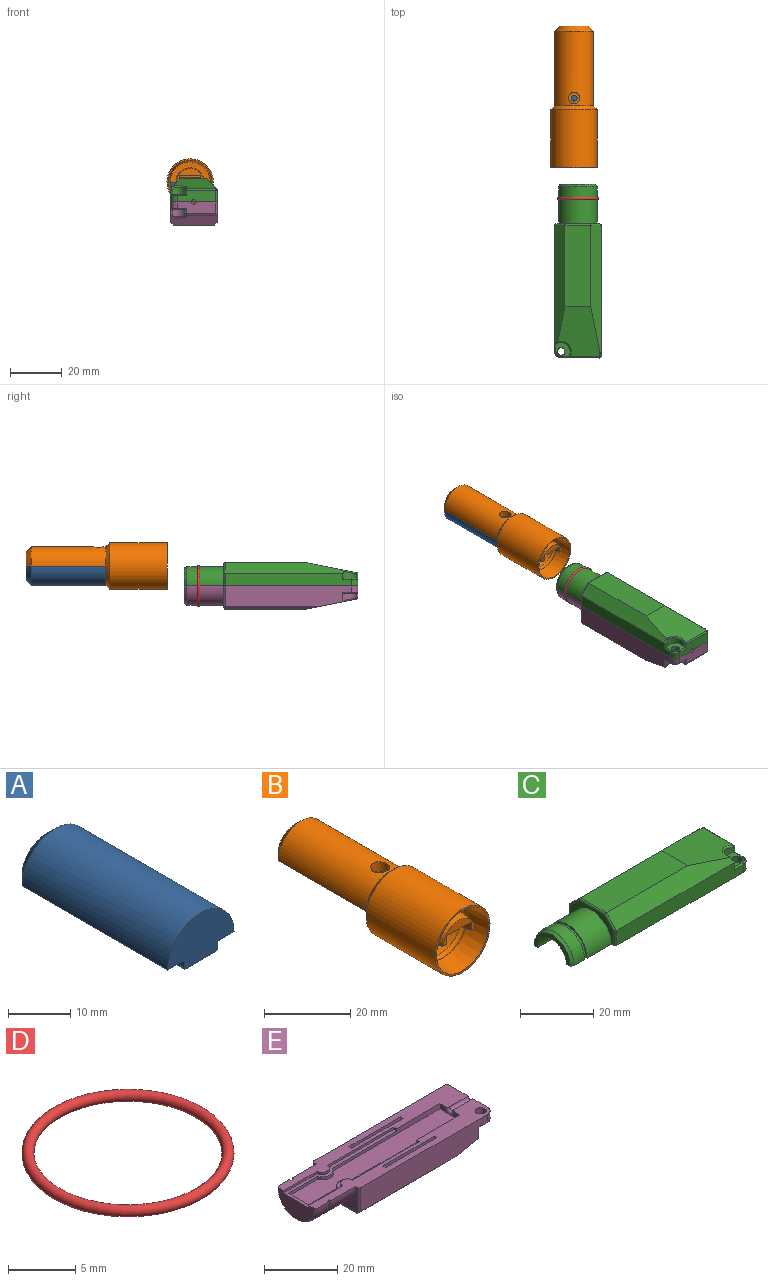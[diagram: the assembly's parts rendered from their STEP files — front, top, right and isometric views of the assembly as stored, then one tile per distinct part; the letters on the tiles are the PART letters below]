
ASSEMBLY  parts=5 mates=4
PART A: 19 faces, bbox 15x35x9.3 mm
  f0: plane 11x5.5mm, normal (0,1,0), area 43mm2, adj f1,f4,f13
  f1: plane 35x15mm, normal (0,0,-1), area 426.5mm2, adj f0,f2,f3,f4,f5,f6,f7,f8
  f2: cylinder r=7.5mm len=33mm, axis (0,1,0), area 777.5mm2, adj f1,f3,f13
  f3: plane 15x9.3mm, normal (0,-1,0), area 101.9mm2, adj f1,f2,f5,f6,f12,f17,f18
  f4: cylinder r=1.7mm len=17mm, axis (0,1,0), area 85mm2, adj f0,f1,f14
  f5: plane 11x1.2mm, normal (1,0,0), area 13.2mm2, adj f1,f3,f11,f18
  f6: plane 11x1.2mm, normal (-1,0,0), area 13.2mm2, adj f1,f3,f7,f17
  f7: plane 1.8x1mm, normal (0,1,0), area 1.7mm2, adj f1,f6,f8,f12,f17
  f8: plane 9x1.8mm, normal (1,0,0), area 16.2mm2, adj f1,f7,f9,f12
  f9: plane 5.6x1.8mm, normal (0,1,0), area 10.1mm2, adj f1,f8,f10,f12
  f10: plane 9x1.8mm, normal (-1,0,0), area 16.2mm2, adj f1,f9,f11,f12
  f11: plane 1.8x1mm, normal (0,1,0), area 1.7mm2, adj f1,f5,f10,f12,f18
  f12: plane 11x7.2mm, normal (0,0,-1), area 28.8mm2, adj f3,f7,f8,f9,f10,f11,f17,f18
  f13: cone r=7.5mm half-angle=45deg, axis (0,-1,0), area 57.8mm2, adj f0,f1,f2
  f14: plane 3.4x1.7mm, normal (0,0.71,-0.71), area 6.4mm2, adj f1,f4
  f15: cylinder r=1.05mm len=6mm, axis (0,0,-1), area 39.6mm2, adj f1,f16
  f16: plane 2.1x2.1mm, normal (0,0,-1), area 3.5mm2, adj f15
  f17: plane 11x0.6mm, normal (-0.95,0,-0.32), area 7mm2, adj f3,f6,f7,f12
  f18: plane 11x0.6mm, normal (0.95,0,-0.32), area 7mm2, adj f3,f5,f11,f12
PART B: 29 faces, bbox 18x54.9x18 mm
  f0: plane 15.6x15.6mm, normal (0,-1,0), area 52.9mm2, adj f4,f7,f8,f21,f28
  f1: cone r=9mm half-angle=45deg, axis (0,-1,0), area 106.6mm2, adj f3,f4,f7,f20,f28
  f2: cylinder r=1.7mm len=8.6mm, axis (0,1,0), area 45.1mm2, adj f4,f5,f7,f11,f25
  f3: cylinder r=7.5mm len=28.9mm, axis (0,1,0), area 665.5mm2, adj f1,f4,f7,f13,f15
  f4: plane 50.7x5.9mm, normal (0,0,-1), area 174.5mm2, adj f0,f1,f2,f3,f5,f8,f9,f11
  f5: plane 11x5.5mm, normal (0,1,0), area 43mm2, adj f2,f4,f7,f13
  f6: plane 10.38x4.9mm, normal (0,-1,0), area 20.2mm2, adj f9,f10,f12,f17,f18,f19
  f7: plane 50.7x5.9mm, normal (0,0,-1), area 174.5mm2, adj f0,f1,f2,f3,f5,f8,f10,f11
  f8: cylinder r=5.5mm len=11mm, axis (0,1,0), area 186.6mm2, adj f0,f4,f7,f17
  f9: plane 45.1x2.7mm, normal (-1,0,0), area 121.3mm2, adj f4,f6,f11,f12,f18
  f10: plane 45.1x2.7mm, normal (1,0,0), area 121.3mm2, adj f6,f7,f11,f12,f19
  f11: plane 8x2.7mm, normal (0,-1,0), area 17.1mm2, adj f2,f4,f7,f9,f10,f12
  f12: plane 45.1x8mm, normal (0,0,-1), area 356.6mm2, adj f6,f9,f10,f11,f14
  f13: cone r=7.5mm half-angle=45deg, axis (0,-1,0), area 57.8mm2, adj f3,f4,f5,f7
  f14: cylinder r=1.15mm len=2.3mm, axis (0,0,-1), area 14.5mm2, adj f12,f16
  f15: cylinder r=2.2mm len=4.4mm, axis (0,0,-1), area 36.4mm2, adj f3,f16
  f16: plane 4.4x4.4mm, normal (0,0,1), area 11.1mm2, adj f14,f15
  f17: cone r=5.2mm half-angle=5.7deg, axis (0,1,0), area 49.8mm2, adj f6,f8,f18,f19
  f18: plane 3.01x1.51mm, normal (0,-0.1,-1), area 4.1mm2, adj f4,f6,f9,f17
  f19: plane 3.01x1.51mm, normal (0,-0.1,-1), area 4.1mm2, adj f6,f7,f10,f17
  f20: cylinder r=9mm len=22.5mm, axis (0,-1,0), area 1272.3mm2, adj f1,f24
  f21: cylinder r=7.8mm len=15.6mm, axis (0,-1,0), area 358.8mm2, adj f0,f22
  f22: torus R=7.3mm, axis (0,-1,0), area 85.6mm2, adj f21,f23
  f23: cone r=8.5mm half-angle=5.2deg, axis (0,-1,0), area 322.7mm2, adj f22,f24
  f24: plane 18x18mm, normal (0,-1,0), area 27.5mm2, adj f20,f23
  f25: cylinder r=0.5mm len=1mm, axis (0,0,1), area 1.5mm2, adj f2,f27
  f26: plane 0.4x0.4mm, normal (0,0,-1), area 0.1mm2, adj f27
  f27: cone r=0.2mm half-angle=45deg, axis (0,0,1), area 0.9mm2, adj f25,f26
  f28: cylinder r=7.6mm len=15.2mm, axis (0,-1,0), area 212.5mm2, adj f0,f1,f4,f7
PART C: 64 faces, bbox 67.6x18.2x10 mm
  f0: plane 67.4x18mm, normal (0,0,-1), area 609.6mm2, adj f2,f3,f4,f6,f7,f9,f10,f11
  f1: plane 5.5x5.5mm, normal (0,0,1), area 18.9mm2, adj f53,f54,f56,f57,f59,f61,f63
  f2: plane 45.1x2.2mm, normal (0,-1,0), area 99.2mm2, adj f0,f17,f18,f52
  f3: cylinder r=7.5mm len=15mm, axis (1,0,0), area 221.5mm2, adj f0,f4,f31
  f4: plane 17x8.5mm, normal (-1,0,0), area 42.4mm2, adj f0,f3,f42,f43,f44,f45,f46
  f5: plane 31.5x10mm, normal (0,0,1), area 315mm2, adj f8,f12,f13,f44
  f6: plane 49x5mm, normal (0,-1,0), area 236.3mm2, adj f0,f13,f45,f55,f56,f57
  f7: plane 51x5mm, normal (0,1,0), area 254.6mm2, adj f0,f12,f42,f47,f49
  f8: plane 19.62x16.25mm, normal (0.2,0,0.98), area 246.1mm2, adj f5,f12,f13,f48,f49,f58,f60
  f9: plane 15x4.59mm, normal (1,0,0), area 60.3mm2, adj f0,f19,f47,f48,f55,f61,f63
  f10: cylinder r=7.5mm len=15mm, axis (1,0,0), area 94.2mm2, adj f0,f32,f51
  f11: plane 14x7mm, normal (-1,0,0), area 29.5mm2, adj f0,f14,f51
  f12: plane 50.02x4mm, normal (0,0.71,0.71), area 234.4mm2, adj f5,f7,f8,f43,f49
  f13: plane 45.62x4mm, normal (0,-0.71,0.71), area 229.4mm2, adj f5,f6,f8,f46,f56,f58
  f14: cylinder r=5.5mm len=12.8mm, axis (-1,0,0), area 221.2mm2, adj f0,f11,f15
  f15: plane 11x5.5mm, normal (-1,0,0), area 47.5mm2, adj f0,f14
  f16: plane 45.1x2.2mm, normal (0,1,0), area 99.2mm2, adj f0,f17,f18,f52
  f17: plane 45.1x8mm, normal (0,0,-1), area 360.8mm2, adj f2,f16,f18,f52
  f18: plane 8x2.2mm, normal (-1,0,0), area 13.1mm2, adj f0,f2,f16,f17,f41
  f19: cylinder r=0.9mm len=7.2mm, axis (-1,0,0), area 20.4mm2, adj f0,f9,f41
  f20: plane 0.8x0.8mm, normal (-1,0,0), area 0.6mm2, adj f0,f21,f23,f38
  f21: plane 19.4x0.8mm, normal (0,1,0), area 15.5mm2, adj f0,f20,f22,f37
  f22: plane 0.8x0.8mm, normal (1,0,0), area 0.6mm2, adj f0,f21,f23,f39
  f23: plane 19.4x0.8mm, normal (0,-1,0), area 15.5mm2, adj f0,f20,f22,f40
  f24: plane 19x0.4mm, normal (0,0,-1), area 7.6mm2, adj f37,f38,f39,f40
  f25: plane 0.8x0.8mm, normal (-1,0,0), area 0.6mm2, adj f0,f26,f28,f34
  f26: plane 19.4x0.8mm, normal (0,1,0), area 15.5mm2, adj f0,f25,f27,f33
  f27: plane 0.8x0.8mm, normal (1,0,0), area 0.6mm2, adj f0,f26,f28,f35
  f28: plane 19.4x0.8mm, normal (0,-1,0), area 15.5mm2, adj f0,f25,f27,f36
  f29: plane 19x0.4mm, normal (0,0,-1), area 7.6mm2, adj f33,f34,f35,f36
  f30: cylinder r=7mm len=14mm, axis (-1,0,0), area 22mm2, adj f0,f31,f32
  f31: plane 15x7.5mm, normal (-1,0,0), area 11.4mm2, adj f0,f3,f30
  f32: plane 15x7.5mm, normal (1,0,0), area 11.4mm2, adj f0,f10,f30
  f33: plane 19.4x0.2mm, normal (0,0.71,-0.71), area 5.4mm2, adj f26,f29,f34,f35
  f34: plane 0.8x0.2mm, normal (-0.71,0,-0.71), area 0.2mm2, adj f25,f29,f33,f36
  f35: plane 0.8x0.2mm, normal (0.71,0,-0.71), area 0.2mm2, adj f27,f29,f33,f36
  f36: plane 19.4x0.2mm, normal (0,-0.71,-0.71), area 5.4mm2, adj f28,f29,f34,f35
  f37: plane 19.4x0.2mm, normal (0,0.71,-0.71), area 5.4mm2, adj f21,f24,f38,f39
  f38: plane 0.8x0.2mm, normal (-0.71,0,-0.71), area 0.2mm2, adj f20,f24,f37,f40
  f39: plane 0.8x0.2mm, normal (0.71,0,-0.71), area 0.2mm2, adj f22,f24,f37,f40
  f40: plane 19.4x0.2mm, normal (0,-0.71,-0.71), area 5.4mm2, adj f23,f24,f38,f39
  f41: torus R=1.7mm, axis (-1,0,0), area 4.7mm2, adj f0,f18,f19
  f42: cylinder r=0.5mm len=5mm, axis (0,0,1), area 3.8mm2, adj f0,f4,f7,f43
  f43: cylinder r=0.5mm len=4.35mm, axis (0,-0.71,0.71), area 4.3mm2, adj f4,f12,f42,f44
  f44: cylinder r=0.5mm len=10mm, axis (0,1,0), area 7.7mm2, adj f4,f5,f43,f46
  f45: cylinder r=0.5mm len=5mm, axis (0,0,-1), area 3.8mm2, adj f0,f4,f6,f46
  f46: cylinder r=0.5mm len=4.35mm, axis (0,-0.71,-0.71), area 4.3mm2, adj f4,f13,f44,f45
  f47: cylinder r=0.5mm len=4.59mm, axis (0,0,-1), area 3.6mm2, adj f0,f7,f9,f50
  f48: cylinder r=0.5mm len=11.54mm, axis (0,1,0), area 7.9mm2, adj f8,f9,f50,f62
  f49: cylinder r=0.5mm len=2.2mm, axis (0.98,0,-0.2), area 1.1mm2, adj f7,f8,f12,f50
  f50: sphere r=0.5mm, area 0.5mm2, adj f47,f48,f49
  f51: cone r=7mm half-angle=26.6deg, axis (1,0,0), area 25.5mm2, adj f0,f10,f11
  f52: plane 8x2.2mm, normal (1,0,0), area 17.6mm2, adj f0,f2,f16,f17
  f53: cylinder r=3.5mm len=5.25mm, axis (0,0,1), area 20mm2, adj f1,f56,f58,f60,f63
  f54: cylinder r=1.5mm len=3mm, axis (0,0,1), area 28.3mm2, adj f0,f1
  f55: cylinder r=2.5mm len=2.5mm, axis (0,0,1), area 9.8mm2, adj f0,f6,f9,f59
  f56: cylinder r=0.5mm len=2.52mm, axis (0,0,1), area 2.2mm2, adj f1,f6,f13,f53,f57,f58
  f57: cylinder r=0.5mm len=3.46mm, axis (-1,0,0), area 2.5mm2, adj f1,f6,f56,f59
  f58: bspline ~1.75x1.64mm, area 1.5mm2, adj f8,f13,f53,f56,f60
  f59: torus R=2mm, axis (0,0,1), area 2.9mm2, adj f1,f55,f57,f61
  f60: bspline ~6x5.21mm, area 6.6mm2, adj f8,f53,f58,f62
  f61: cylinder r=0.5mm len=3.46mm, axis (0,-1,0), area 2.5mm2, adj f1,f9,f59,f63
  f62: sphere r=0.5mm, area 0.5mm2, adj f48,f60,f63
  f63: cylinder r=0.5mm len=2.09mm, axis (0,0,1), area 1.9mm2, adj f1,f9,f53,f61,f62
PART D: 1 faces, bbox 17.1x17.1x0.9 mm
  f0: torus R=7.45mm, axis (0,0,-1), area 130.8mm2
PART E: 65 faces, bbox 67.6x18.2x9 mm
  f0: plane 67.4x8.1mm, normal (0,0,1), area 280.3mm2, adj f1,f2,f5,f6,f8,f9,f13,f17
  f1: plane 49x8mm, normal (0,-1,0), area 364.8mm2, adj f0,f12,f14,f47,f57,f58,f59
  f2: plane 15x4.59mm, normal (1,0,0), area 60.3mm2, adj f0,f4,f50,f51,f53,f57,f63,f64
  f3: plane 5.5x5.5mm, normal (0,0,-1), area 18.9mm2, adj f55,f56,f58,f59,f61,f63,f64
  f4: plane 67.4x8.1mm, normal (0,0,1), area 288.7mm2, adj f2,f5,f6,f8,f9,f11,f13,f16
  f5: plane 7.6x1.8mm, normal (-1,0,0), area 9.1mm2, adj f0,f4,f21,f22,f31,f54
  f6: cylinder r=7.5mm len=15mm, axis (1,0,0), area 221.5mm2, adj f0,f4,f9,f43
  f7: plane 42.6x9.8mm, normal (0,0,1), area 101.8mm2, adj f8,f16,f17,f18,f19,f20,f21,f22
  f8: plane 14x7mm, normal (-1,0,0), area 69.1mm2, adj f0,f4,f7,f16,f17,f52
  f9: plane 17x8.5mm, normal (-1,0,0), area 55.6mm2, adj f0,f4,f6,f45,f46,f47,f48,f49
  f10: plane 31.5x16mm, normal (0,0,-1), area 504mm2, adj f12,f14,f15,f48
  f11: plane 51x8mm, normal (0,1,0), area 387mm2, adj f4,f12,f15,f45,f50
  f12: plane 19.6x18.01mm, normal (0.2,0,-0.98), area 319.4mm2, adj f1,f10,f11,f14,f15,f50,f51,f58
  f13: cylinder r=7.5mm len=15mm, axis (1,0,0), area 94.2mm2, adj f0,f4,f44,f52
  f14: plane 36.5x1mm, normal (0,-0.71,-0.71), area 48.1mm2, adj f1,f10,f12,f49
  f15: plane 36.5x1mm, normal (0,0.71,-0.71), area 48.1mm2, adj f10,f11,f12,f46
  f16: plane 13.05x0.8mm, normal (0,-1,0), area 10.4mm2, adj f4,f7,f8,f25
  f17: plane 13.05x0.8mm, normal (0,1,0), area 10.4mm2, adj f0,f7,f8,f18
  f18: cylinder r=1.95mm len=3.9mm, axis (0,0,1), area 4.9mm2, adj f0,f7,f17,f19
  f19: plane 25.65x0.8mm, normal (0,1,0), area 20.5mm2, adj f0,f7,f18,f20
  f20: plane 1.1x0.8mm, normal (-1,0,0), area 0.9mm2, adj f0,f7,f19,f21
  f21: plane 41.66x1.8mm, normal (0,1,0), area 55.1mm2, adj f0,f5,f7,f20,f30,f31
  f22: plane 41.66x1.8mm, normal (0,-1,0), area 55.1mm2, adj f4,f5,f7,f23,f26,f31
  f23: plane 1.1x0.8mm, normal (-1,0,0), area 0.9mm2, adj f4,f7,f22,f24
  f24: plane 25.65x0.8mm, normal (0,-1,0), area 20.5mm2, adj f4,f7,f23,f25
  f25: cylinder r=1.95mm len=3.9mm, axis (0,0,1), area 4.9mm2, adj f4,f7,f16,f24
  f26: cylinder r=2.95mm len=5.51mm, axis (0,0,1), area 7.1mm2, adj f7,f22,f27,f31
  f27: plane 11.22x1mm, normal (0,-1,0), area 11.2mm2, adj f7,f26,f28,f31
  f28: plane 7.8x1mm, normal (1,0,0), area 7.8mm2, adj f7,f27,f29,f31
  f29: plane 11.22x1mm, normal (0,1,0), area 11.2mm2, adj f7,f28,f30,f31
  f30: cylinder r=2.95mm len=5.51mm, axis (0,0,1), area 7.1mm2, adj f7,f21,f29,f31
  f31: plane 58.4x7.8mm, normal (0,0,1), area 431.4mm2, adj f5,f21,f22,f26,f27,f28,f29,f30
  f32: plane 20x1.2mm, normal (0,-1,0), area 24mm2, adj f0,f33,f35,f36
  f33: plane 1.2x1mm, normal (1,0,0), area 1.2mm2, adj f0,f32,f34,f36
  f34: plane 20x1.2mm, normal (0,1,0), area 24mm2, adj f0,f33,f35,f36
  f35: plane 1.2x1mm, normal (-1,0,0), area 1.2mm2, adj f0,f32,f34,f36
  f36: plane 20x1mm, normal (0,0,1), area 20mm2, adj f32,f33,f34,f35
  f37: plane 20x1.2mm, normal (0,-1,0), area 24mm2, adj f4,f38,f40,f41
  f38: plane 1.2x1mm, normal (1,0,0), area 1.2mm2, adj f4,f37,f39,f41
  f39: plane 20x1.2mm, normal (0,1,0), area 24mm2, adj f4,f38,f40,f41
  f40: plane 1.2x1mm, normal (-1,0,0), area 1.2mm2, adj f4,f37,f39,f41
  f41: plane 20x1mm, normal (0,0,1), area 20mm2, adj f37,f38,f39,f40
  f42: cylinder r=7mm len=14mm, axis (-1,0,0), area 22mm2, adj f0,f4,f43,f44
  f43: plane 15x7.5mm, normal (-1,0,0), area 11.4mm2, adj f0,f4,f6,f42
  f44: plane 15x7.5mm, normal (1,0,0), area 11.4mm2, adj f0,f4,f13,f42
  f45: cylinder r=0.5mm len=8mm, axis (0,0,1), area 6.2mm2, adj f4,f9,f11,f46
  f46: cylinder r=0.5mm len=1.35mm, axis (0,0.71,0.71), area 0.9mm2, adj f9,f15,f45,f48
  f47: cylinder r=0.5mm len=8mm, axis (0,0,-1), area 6.2mm2, adj f0,f1,f9,f49
  f48: cylinder r=0.5mm len=16mm, axis (0,-1,0), area 12.4mm2, adj f9,f10,f46,f49
  f49: cylinder r=0.5mm len=1.35mm, axis (0,0.71,-0.71), area 0.9mm2, adj f9,f14,f47,f48
  f50: cylinder r=0.5mm len=5.1mm, axis (0,0,-1), area 3.9mm2, adj f2,f4,f11,f12,f51
  f51: cylinder r=0.5mm len=12.03mm, axis (0,-1,0), area 8.1mm2, adj f2,f12,f50,f62
  f52: cone r=7mm half-angle=26.6deg, axis (1,0,0), area 25.5mm2, adj f0,f4,f8,f13
  f53: cylinder r=0.9mm len=7.2mm, axis (1,0,0), area 20.4mm2, adj f0,f2,f4,f54
  f54: torus R=1.7mm, axis (-1,0,0), area 4.7mm2, adj f0,f4,f5,f53
  f55: cylinder r=3.5mm len=5.25mm, axis (0,0,-1), area 19.6mm2, adj f3,f58,f60,f64
  f56: cylinder r=1.5mm len=3mm, axis (0,0,-1), area 28.3mm2, adj f0,f3
  f57: cylinder r=2.5mm len=2.5mm, axis (0,0,-1), area 9.8mm2, adj f0,f1,f2,f61
  f58: cylinder r=0.5mm len=3.69mm, axis (0,0,-1), area 3.3mm2, adj f1,f3,f12,f55,f59,f60
  f59: cylinder r=0.5mm len=3.46mm, axis (1,0,0), area 2.5mm2, adj f1,f3,f58,f61
  f60: bspline ~6.37x6mm, area 7.3mm2, adj f12,f55,f58,f62
  f61: torus R=2mm, axis (0,0,-1), area 2.9mm2, adj f3,f57,f59,f63
  f62: sphere r=0.5mm, area 0.5mm2, adj f51,f60,f64
  f63: cylinder r=0.5mm len=3.46mm, axis (0,1,0), area 2.5mm2, adj f2,f3,f61,f64
  f64: cylinder r=0.5mm len=2.09mm, axis (0,0,-1), area 1.9mm2, adj f2,f3,f55,f62,f63
PLACE A rot(axis=(0,-1,0),180deg) t=(-31.39,-50.09,14)mm
PLACE B t=(-31.39,-50.09,14)mm
PLACE C rot(axis=(0,0,-1),90deg) t=(-29.95,-152.92,-2.73)mm
PLACE D rot(axis=(-1,0,0),90deg) t=(-29.95,-117.02,6.27)mm
PLACE E rot(axis=(0,0,-1),90deg) t=(-29.95,-152.92,-2.73)mm fixed
MATE fastened E.f4 <-> C.f0  axis (0,0,-1) through (-20.95,-178.42,6.27)mm
MATE revolute C.f3 <-> D.f0  axis (0,1,0) through (-29.95,-117.02,6.27)mm
MATE cylindrical C.f3 <-> D.f0  axis (0,1,0) through (-29.95,-111.52,6.27)mm
MATE fastened A.f1 <-> B.f4  axis (0,0,-1) through (-29.69,-50.09,14)mm
